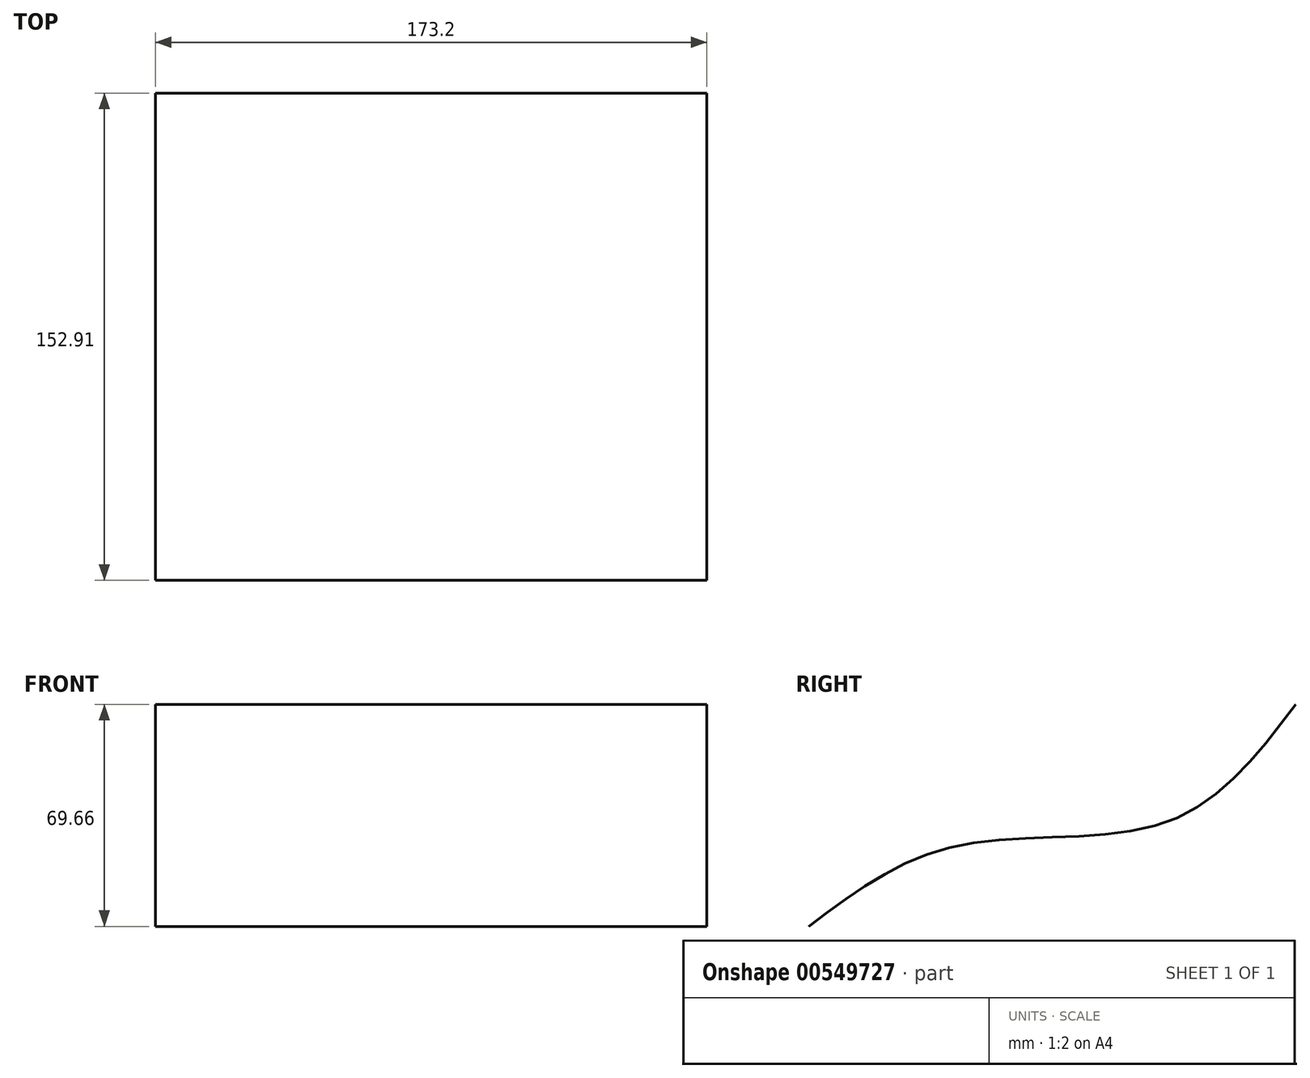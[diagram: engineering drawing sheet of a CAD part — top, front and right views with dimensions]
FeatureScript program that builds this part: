
annotation { "Feature Type Name" : "Feature", "Feature Type Description" : "" }
export const myFeature = defineFeature(function(context is Context, id is Id, definition is map)
    precondition{}
    {
        {
            var Q0;
            Q0=qCreatedBy(makeId("Right.planeOp"),FACE);
            var sketch = newSketch(context, id + "F0", { "sketchPlane" : qUnion([Q0])});
            skFitSpline(sketch, "E0", {"points": [v(-50.04, 0) * mm, v(-3.28, 25.36) * mm, v(62.26, 32.74) * mm, v(102.87, 69.66) * mm], "startDerivative": vector(132.8, 100.42) * mm, "endDerivative": vector(107.42, 141.51) * mm});
            skSolve(sketch);
        }
        {
            var Q0;
            Q0=sQuery(id+"F0.wireOp",EDGE,"E0");
            extrude(context, id + "F1", {"bodyType" : ToolBodyType.SURFACE, "surfaceEntities" : qUnion([Q0]), "endBound" : BoundingType.SYMMETRIC, "depth" : 173.2 * mm, "offsetDistance" : 25 * mm});
        }
    });
